annotation { "Feature Type Name" : "Feature", "Feature Type Description" : "" }
export const myFeature = defineFeature(function(context is Context, id is Id, definition is map)
    precondition{}
    {
        {
            var Q0;
            Q0=qCreatedBy(makeId("Top.planeOp"),FACE);
            var sketch = newSketch(context, id + "F0", { "sketchPlane" : qUnion([Q0])});
            skLineSegment(sketch, "E0.bottom", {"start": v(-55.12, 47.97) * mm, "end": v(46.48, 47.97) * mm});
            skLineSegment(sketch, "E0.top", {"start": v(-55.12, -53.63) * mm, "end": v(46.48, -53.63) * mm});
            skLineSegment(sketch, "E0.left", {"start": v(-55.12, 47.97) * mm, "end": v(-55.12, -53.63) * mm});
            skLineSegment(sketch, "E0.right", {"start": v(46.48, 47.97) * mm, "end": v(46.48, -53.63) * mm});
            skLineSegment(sketch, "E1.bottom", {"start": v(46.48, -53.63) * mm, "end": v(46.48, -53.63) * mm});
            skLineSegment(sketch, "E1.top", {"start": v(46.48, 47.97) * mm, "end": v(46.48, 47.97) * mm});
            skLineSegment(sketch, "E1.left", {"start": v(46.48, -53.63) * mm, "end": v(46.48, 47.97) * mm});
            skLineSegment(sketch, "E1.right", {"start": v(46.48, -53.63) * mm, "end": v(46.48, 47.97) * mm});
            skSolve(sketch);
        }
        {
            var Q0;
            Q0 = qSketchRegion(id + "F0", true);
            extrude(context, id + "F1", {"entities" : qUnion([Q0]), "depth" : 101.6 * mm});
        }
        {
            var Q0;
            Q0=makeQuery(id+"F1.opExtrude","SWEPT_FACE",FACE,{"disambiguationData":[OSD([sQuery(id+"F0.wireOp",EDGE,"E0.top")])]});
            var sketch = newSketch(context, id + "F2", { "sketchPlane" : qUnion([Q0])});
            skLineSegment(sketch, "E2", {"start": v(-7.72, 72.8) * mm, "end": v(-30.9, 33.18) * mm});
            skLineSegment(sketch, "E3", {"start": v(-7.72, 72.8) * mm, "end": v(14.77, 33.18) * mm});
            skLineSegment(sketch, "E4", {"start": v(-30.9, 33.18) * mm, "end": v(14.77, 33.18) * mm});
            skSolve(sketch);
        }
        {
            var Q0;
            Q0 = qSketchRegion(id + "F2", true);
            extrude(context, id + "F3", {"entities" : qUnion([Q0]), "operationType" : NewBodyOperationType.REMOVE, "oppositeDirection" : true, "depth" : 101.6 * mm});
        }
        {
            var Q0;
            Q0=makeQuery(id+"F1.opExtrude","CAP_FACE",FACE,{"disambiguationData":[OSD([sQuery(id+"F0.wireOp",EDGE,"E0.bottom"),sQuery(id+"F0.wireOp",EDGE,"E0.top"),sQuery(id+"F0.wireOp",EDGE,"E0.left"),sQuery(id+"F0.wireOp",EDGE,"E1.right")])],"isStart":false});
            var sketch = newSketch(context, id + "F4", { "sketchPlane" : qUnion([Q0])});
            skText(sketch, "E5", { "text": "Great Cube", "fontName": "RobotoSlab-Regular.ttf"});
            const initialGuessF4  = {"E5": [-0.05582, -0.00585, 1, 0, 0.01414]};
            skSetInitialGuess(sketch, initialGuessF4);
            skSolve(sketch);
        }
        {
            var Q0;
            Q0 = qSketchRegion(id + "F4", true);
            extrude(context, id + "F5", {"entities" : qUnion([Q0]), "operationType" : NewBodyOperationType.ADD, "depth" : 3.17 * mm});
        }
        {
            var Q0;
            Q0=makeQuery(id+"F1.opExtrude","CAP_FACE",FACE,{"disambiguationData":[OSD([sQuery(id+"F0.wireOp",EDGE,"E0.bottom"),sQuery(id+"F0.wireOp",EDGE,"E0.top"),sQuery(id+"F0.wireOp",EDGE,"E0.left"),sQuery(id+"F0.wireOp",EDGE,"E1.right")])],"isStart":true});
            var sketch = newSketch(context, id + "F6", { "sketchPlane" : qUnion([Q0])});
            skText(sketch, "E6", { "text": "Great Cube", "fontName": "RobotoSlab-Regular.ttf"});
            const initialGuessF6  = {"E6": [-0.054, -0.00526, 1, 0, 0.01414]};
            skSetInitialGuess(sketch, initialGuessF6);
            skSolve(sketch);
        }
        {
            var Q0;
            Q0 = qSketchRegion(id + "F6", true);
            extrude(context, id + "F7", {"entities" : qUnion([Q0]), "operationType" : NewBodyOperationType.REMOVE, "oppositeDirection" : true, "depth" : 101.35 * mm});
        }
    });